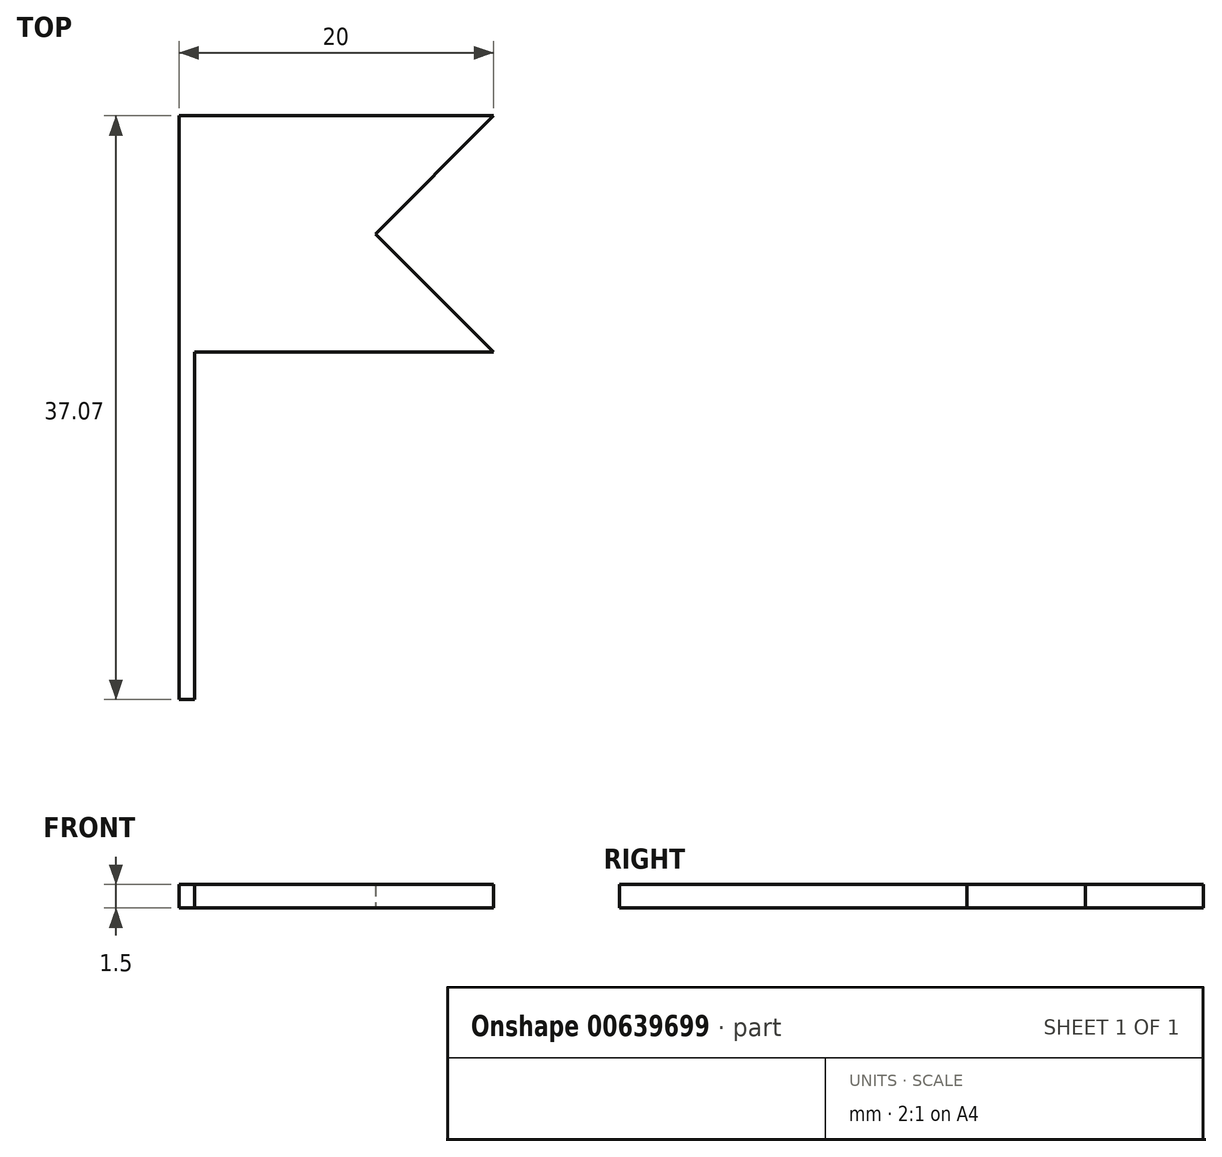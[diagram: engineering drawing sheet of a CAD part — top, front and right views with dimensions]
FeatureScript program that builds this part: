
annotation { "Feature Type Name" : "Feature", "Feature Type Description" : "" }
export const myFeature = defineFeature(function(context is Context, id is Id, definition is map)
    precondition{}
    {
        {
            var Q0;
            Q0=qCreatedBy(makeId("Top.planeOp"),FACE);
            var sketch = newSketch(context, id + "F0", { "sketchPlane" : qUnion([Q0])});
            skLineSegment(sketch, "E0", {"start": v(0, 0) * mm, "end": v(20, 0) * mm});
            skLineSegment(sketch, "E1", {"start": v(20, -15) * mm, "end": v(0, -15) * mm});
            skLineSegment(sketch, "E2", {"start": v(0, -15) * mm, "end": v(0, 0) * mm});
            skLineSegment(sketch, "E3", {"start": v(20, 0) * mm, "end": v(12.5, -7.5) * mm});
            skLineSegment(sketch, "E4", {"start": v(12.5, -7.5) * mm, "end": v(20, -15) * mm});
            skLineSegment(sketch, "E5", {"start": v(0, -15) * mm, "end": v(0, -37.07) * mm});
            skLineSegment(sketch, "E6", {"start": v(0, -37.07) * mm, "end": v(1, -37.07) * mm});
            skLineSegment(sketch, "E7", {"start": v(1, -37.07) * mm, "end": v(1, -15) * mm});
            skSolve(sketch);
        }
        {
            var Q0;
            Q0=makeQuery(id+"F0.imprint","IMPRINT",FACE,{"disambiguationData":[TD([[makeQuery(id+"F0.imprint","IMPRINT",EDGE,{"derivedFrom":sQuery(id+"F0.wireOp",EDGE,"E0")}),-1.0]])]});
            var Q1;
            {var subQ0=sQuery(id+"F0.wireOp",EDGE,"E5");Q1=makeQuery(id+"F0.imprint","IMPRINT",FACE,{"disambiguationData":[TD([[makeQuery(id+"F0.imprint","IMPRINT",EDGE,{"derivedFrom":subQ0}),1.0]])]});}
            extrude(context, id + "F1", {"entities" : qUnion([Q0, Q1]), "depth" : 1.5 * mm, "offsetDistance" : 25 * mm});
        }
    });
